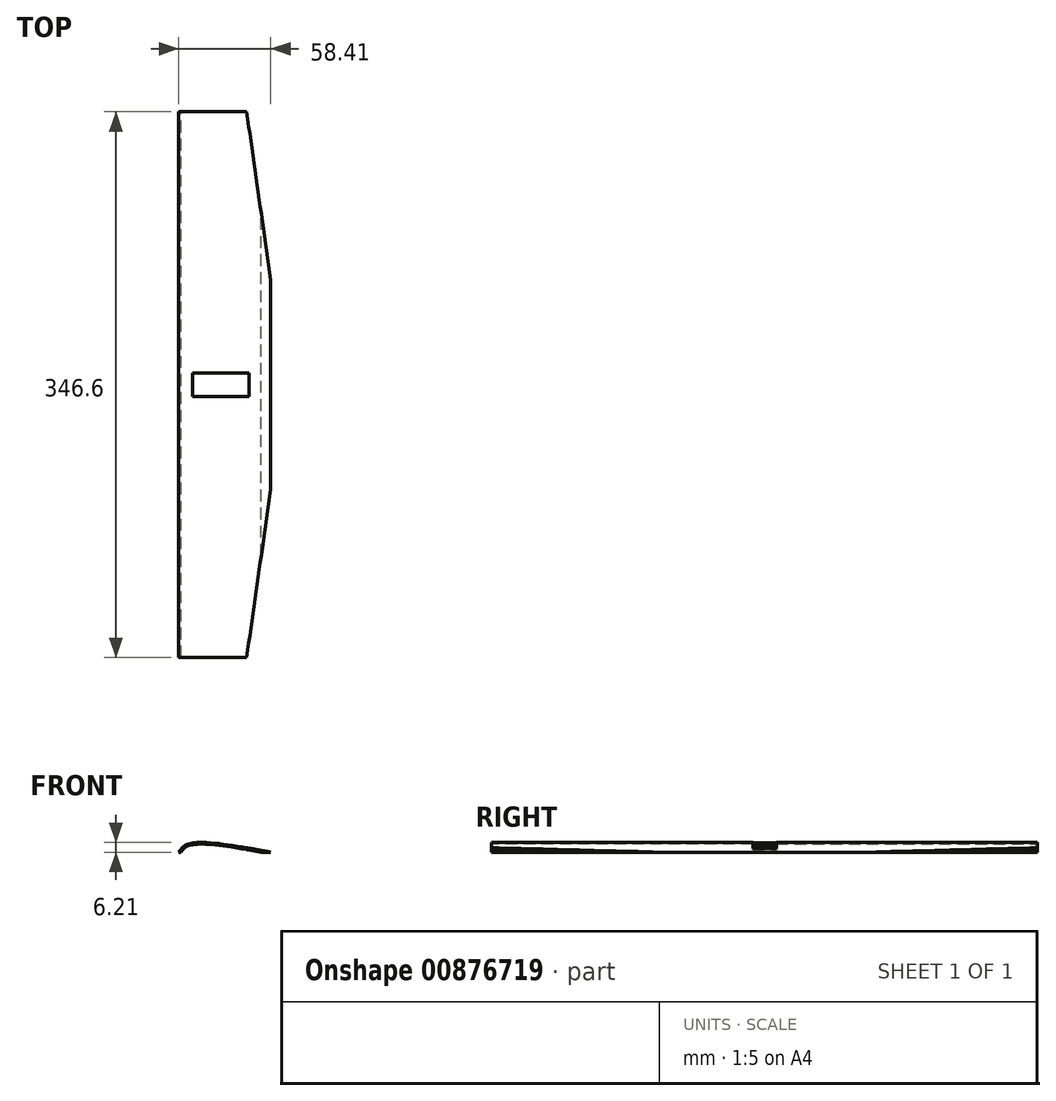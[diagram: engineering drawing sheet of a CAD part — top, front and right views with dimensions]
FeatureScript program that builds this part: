
annotation { "Feature Type Name" : "Feature", "Feature Type Description" : "" }
export const myFeature = defineFeature(function(context is Context, id is Id, definition is map)
    precondition{}
    {
        {
            var Q0;
            Q0=qCreatedBy(makeId("Front.planeOp"),FACE);
            var sketch = newSketch(context, id + "F0", { "sketchPlane" : qUnion([Q0])});
            skFitSpline(sketch, "E0", {"points": [v(-26.6, 0) * mm, v(-20.43, 5.32) * mm, v(31.82, 0) * mm], "startDerivative": vector(14.6, 22.54) * mm, "endDerivative": vector(91.12, -16.83) * mm});
            skLineSegment(sketch, "E1", {"start": v(-26.6, 0) * mm, "end": v(31.82, 0) * mm});
            skSolve(sketch);
        }
        {
            var Q0;
            Q0=makeQuery(id+"F0.imprint","IMPRINT",FACE,{"disambiguationData":[TD([[makeQuery(id+"F0.imprint","IMPRINT",EDGE,{"derivedFrom":sQuery(id+"F0.wireOp",EDGE,"E0")}),-1.0]])]});
            var sketch = newSketch(context, id + "F1", { "sketchPlane" : qUnion([Q0])});
            skFitSpline(sketch, "E2.0", {"points": [v(31.62, -1.08) * mm, v(27.82, -0.38) * mm, v(20.23, 1.02) * mm, v(9.28, 2.9) * mm, v(0.86, 4.12) * mm, v(-5.23, 4.77) * mm, v(-9.43, 5.06) * mm, v(-13.18, 5.15) * mm, v(-15.9, 5.02) * mm, v(-17.8, 4.8) * mm, v(-19.06, 4.56) * mm, v(-20.17, 4.27) * mm, v(-21.43, 3.8) * mm, v(-22.67, 3.06) * mm, v(-23.81, 2) * mm, v(-24.77, 0.78) * mm, v(-25.36, -0.13) * mm, v(-25.67, -0.6) * mm]});
            skLineSegment(sketch, "E2.1", {"start": v(-24.51, 1.1) * mm, "end": v(19.66, 1.1) * mm});
            skSolve(sketch);
        }
        {
            var Q0;
            Q0=makeQuery(id+"F1.imprint","IMPRINT",FACE,{"disambiguationData":[TD([[makeQuery(id+"F1.imprint","IMPRINT",EDGE,{"derivedFrom":sQuery(id+"F1.wireOp",EDGE,"E2.0")}),-1.0]])]});
            extrude(context, id + "F2", {"entities" : qUnion([Q0]), "depth" : 173.3 * mm, "offsetDistance" : 25 * mm});
        }
        {
            var Q0;
            Q0=qCreatedBy(makeId("Top.planeOp"),FACE);
            var sketch = newSketch(context, id + "F3", { "sketchPlane" : qUnion([Q0])});
            skLineSegment(sketch, "E3", {"start": v(42.78, 10) * mm, "end": v(15.9, -177.5) * mm});
            skLineSegment(sketch, "E4", {"start": v(15.9, -177.5) * mm, "end": v(65.33, -177.5) * mm});
            skLineSegment(sketch, "E5", {"start": v(65.33, -177.5) * mm, "end": v(42.78, 10) * mm});
            skSolve(sketch);
        }
        {
            var Q0;
            Q0=makeQuery(id+"F3.imprint","IMPRINT",FACE,{"disambiguationData":[TD([[makeQuery(id+"F3.imprint","IMPRINT",EDGE,{"derivedFrom":sQuery(id+"F3.wireOp",EDGE,"E3")}),1.0]])]});
            extrude(context, id + "F4", {"entities" : qUnion([Q0]), "operationType" : NewBodyOperationType.REMOVE, "oppositeDirection" : true, "depth" : -25 * mm, "offsetDistance" : 25 * mm});
        }
        {
            var Q0;
            Q0=makeQuery(id+"F2.opExtrude","SWEPT_BODY",BODY,{"disambiguationData":[OSD([sQuery(id+"F0.wireOp",EDGE,"E0"),sQuery(id+"F0.wireOp",EDGE,"E1"),sQuery(id+"F1.wireOp",EDGE,"E2.0"),sQuery(id+"F1.wireOp",EDGE,"E2.1")])]});
            var Q1;
            Q1=qCreatedBy(makeId("Front.planeOp"),FACE);
            mirror(context, id + "F5", {"operationType" : NewBodyOperationType.ADD, "entities" : qUnion([Q0]), "mirrorPlane" : qUnion([Q1])});
        }
        {
            var Q0;
            Q0=qCreatedBy(makeId("Top.planeOp"),FACE);
            var sketch = newSketch(context, id + "F6", { "sketchPlane" : qUnion([Q0])});
            skLineSegment(sketch, "E6.bottom", {"start": v(-18, 7.5) * mm, "end": v(18, 7.5) * mm});
            skLineSegment(sketch, "E6.top", {"start": v(-18, -7.5) * mm, "end": v(18, -7.5) * mm});
            skLineSegment(sketch, "E6.left", {"start": v(-18, 7.5) * mm, "end": v(-18, -7.5) * mm});
            skLineSegment(sketch, "E6.right", {"start": v(18, 7.5) * mm, "end": v(18, -7.5) * mm});
            skPoint(sketch, "E6.middle", {"position": v(0, 0) * mm});
            skSolve(sketch);
        }
        {
            var Q0;
            Q0=makeQuery(id+"F6.imprint","IMPRINT",FACE,{"disambiguationData":[TD([[makeQuery(id+"F6.imprint","IMPRINT",EDGE,{"derivedFrom":sQuery(id+"F6.wireOp",EDGE,"E6.bottom")}),-1.0]])]});
            extrude(context, id + "F7", {"entities" : qUnion([Q0]), "operationType" : NewBodyOperationType.REMOVE, "oppositeDirection" : true, "depth" : -20 * mm, "offsetDistance" : 25 * mm});
        }
    });
